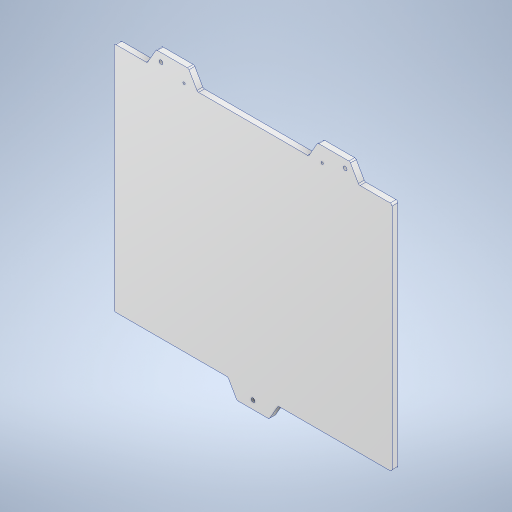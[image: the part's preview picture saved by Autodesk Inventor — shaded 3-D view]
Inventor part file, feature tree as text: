
AUTODESK INVENTOR PART (.ipt)
format: ipt  version: 2024 (Build 280153000, 153)  size: 295,936 bytes
history: native  units: mm
features: sketch x3, extrude x2, hole x2, fillet x1
ambient origin geometry x8: Origin, YZ Plane, XZ Plane, XY Plane, X Axis, Y Axis, Z Axis, Center Point
bodies: Solid1 (feature_tree)
feature tree (8):
  extrude  "Extrusion1"  Depth=252.0mm
  sketch  "Sketch2"  dims[d2=6.35mm d3=0.0mm d4=18.0mm]
  extrude  "Extrusion2"  Depth=6.35mm
  hole  "Hole1"  [1 undecoded]
  fillet  "Fillet1"  Radius=17.0mm
  hole  "Hole2"  [1 undecoded]
  sketch  "Sketch1"  dims[d0=302.0mm d1=252.0mm]
  sketch  "Sketch3"  dims[d5=200.0mm d6=8.0mm d7=17.0mm d8=17.0mm d9=35.0mm d10=8.0mm d11=6.35mm d12=0.0mm d13=4.134mm d14=10.0mm d15=4.0mm d16=2.0mm d17=90.0deg d18=8.0mm d19=20.594885mm d20=2.0mm d21=300.0mm d22=250.0mm d23=3.2mm d24=150.0mm d25=2.459mm d26=6.0mm d27=4.0mm d28=2.0mm d29=90.0deg d30=8.0mm d31=20.594885mm d32=35.0mm d33=35.0mm]
note: 2 required parameter values undecoded (feature->parameter linkage not recoverable at this tier; creation-order binding heuristic only, values carry confidence <= 0.55)
